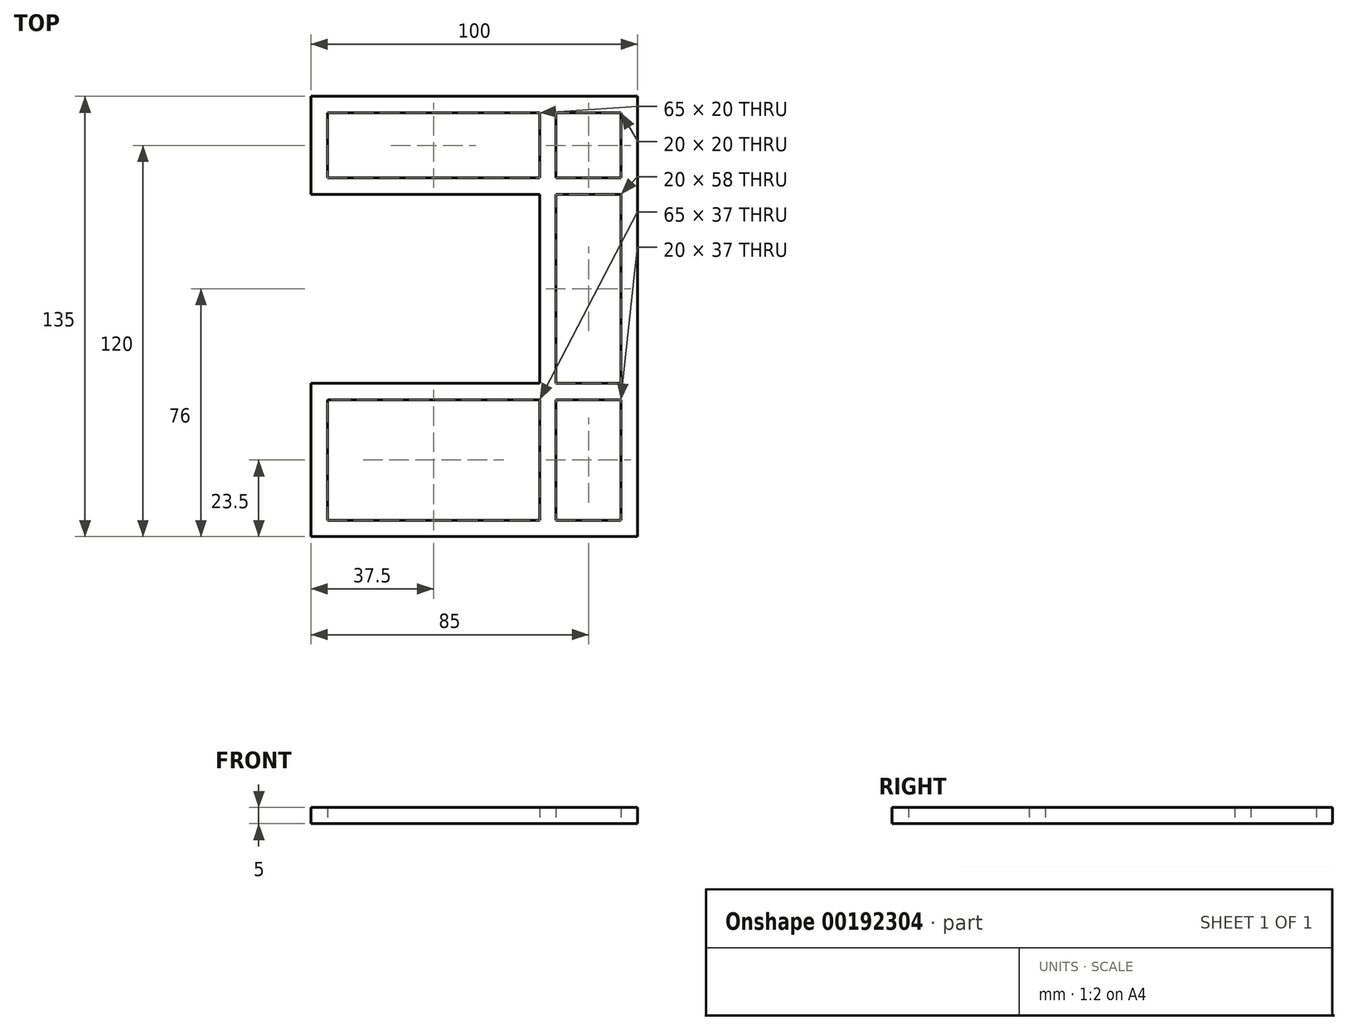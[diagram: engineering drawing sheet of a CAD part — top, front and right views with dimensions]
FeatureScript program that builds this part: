
annotation { "Feature Type Name" : "Feature", "Feature Type Description" : "" }
export const myFeature = defineFeature(function(context is Context, id is Id, definition is map)
    precondition{}
    {
        {
            var Q0;
            Q0=qCreatedBy(makeId("Top.planeOp"),FACE);
            var sketch = newSketch(context, id + "F0", { "sketchPlane" : qUnion([Q0])});
            skLineSegment(sketch, "E0", {"start": v(0, 0) * mm, "end": v(0, 135) * mm});
            skLineSegment(sketch, "E1", {"start": v(0, 135) * mm, "end": v(-100, 135) * mm});
            skLineSegment(sketch, "E2", {"start": v(-100, 135) * mm, "end": v(-100, 105) * mm});
            skLineSegment(sketch, "E3", {"start": v(-100, 105) * mm, "end": v(-30, 105) * mm});
            skLineSegment(sketch, "E4", {"start": v(0, 0) * mm, "end": v(-100, 0) * mm});
            skLineSegment(sketch, "E5", {"start": v(-100, 0) * mm, "end": v(-100, 47) * mm});
            skLineSegment(sketch, "E6", {"start": v(-100, 47) * mm, "end": v(-30, 47) * mm});
            skLineSegment(sketch, "E7", {"start": v(-30, 105) * mm, "end": v(-30, 47) * mm});
            skPoint(sketch, "E8.orphan", {"position": v(0, 47) * mm});
            skLineSegment(sketch, "E9.0", {"start": v(-95, 130) * mm, "end": v(-95, 110) * mm});
            skLineSegment(sketch, "E10.0", {"start": v(-5, 130) * mm, "end": v(-95, 130) * mm});
            skLineSegment(sketch, "E11.0", {"start": v(-5, 5) * mm, "end": v(-5, 130) * mm});
            skLineSegment(sketch, "E12.0", {"start": v(-5, 5) * mm, "end": v(-95, 5) * mm});
            skLineSegment(sketch, "E13.0", {"start": v(-95, 5) * mm, "end": v(-95, 42) * mm});
            skLineSegment(sketch, "E14.0", {"start": v(-95, 42) * mm, "end": v(-30, 42) * mm});
            skLineSegment(sketch, "E15.0", {"start": v(-25, 105) * mm, "end": v(-25, 47) * mm});
            skLineSegment(sketch, "E16.0", {"start": v(-95, 110) * mm, "end": v(-30, 110) * mm});
            skLineSegment(sketch, "E17", {"start": v(-25, 105) * mm, "end": v(-25, 110) * mm});
            skLineSegment(sketch, "E18", {"start": v(-30, 42) * mm, "end": v(-25, 42) * mm});
            skLineSegment(sketch, "E19", {"start": v(-25, 42) * mm, "end": v(-25, 47) * mm});
            skLineSegment(sketch, "E20", {"start": v(-25, 110) * mm, "end": v(-30, 110) * mm});
            skLineSegment(sketch, "E21", {"start": v(-5, 130) * mm, "end": v(-10, 130) * mm});
            skLineSegment(sketch, "E22", {"start": v(-5, 130) * mm, "end": v(-5, 125) * mm});
            skLineSegment(sketch, "E23", {"start": v(-30, 110) * mm, "end": v(-30, 130) * mm});
            skLineSegment(sketch, "E24", {"start": v(-25, 110) * mm, "end": v(-25, 130) * mm});
            skLineSegment(sketch, "E25", {"start": v(-30, 42) * mm, "end": v(-30, 5) * mm});
            skLineSegment(sketch, "E26", {"start": v(-25, 42) * mm, "end": v(-25, 5) * mm});
            skLineSegment(sketch, "E27", {"start": v(-25, 47) * mm, "end": v(-5, 47) * mm});
            skLineSegment(sketch, "E28", {"start": v(-25, 42) * mm, "end": v(-5, 42) * mm});
            skLineSegment(sketch, "E29", {"start": v(-25, 105) * mm, "end": v(-5, 105) * mm});
            skLineSegment(sketch, "E30", {"start": v(-25, 110) * mm, "end": v(-5, 110) * mm});
            skSolve(sketch);
        }
        {
            var Q0;
            Q0=makeQuery(id+"F0.imprint","IMPRINT",FACE,{"disambiguationData":[TD([[makeQuery(id+"F0.imprint","IMPRINT",EDGE,{"derivedFrom":sQuery(id+"F0.wireOp",EDGE,"E0")}),1.0]])]});
            var Q1;
            Q1=makeQuery(id+"F0.imprint","IMPRINT",FACE,{"disambiguationData":[TD([[makeQuery(id+"F0.imprint","IMPRINT",EDGE,{"derivedFrom":sQuery(id+"F0.wireOp",EDGE,"E20")}),-1.0]])]});
            var Q2;
            Q2=makeQuery(id+"F0.imprint","IMPRINT",FACE,{"disambiguationData":[TD([[makeQuery(id+"F0.imprint","IMPRINT",EDGE,{"derivedFrom":sQuery(id+"F0.wireOp",EDGE,"E17")}),-1.0]])]});
            var Q3;
            Q3=makeQuery(id+"F0.imprint","IMPRINT",FACE,{"disambiguationData":[TD([[makeQuery(id+"F0.imprint","IMPRINT",EDGE,{"derivedFrom":sQuery(id+"F0.wireOp",EDGE,"E19")}),-1.0]])]});
            var Q4;
            Q4=makeQuery(id+"F0.imprint","IMPRINT",FACE,{"disambiguationData":[TD([[makeQuery(id+"F0.imprint","IMPRINT",EDGE,{"derivedFrom":sQuery(id+"F0.wireOp",EDGE,"E18")}),-1.0]])]});
            extrude(context, id + "F1", {"entities" : qUnion([Q0, Q1, Q2, Q3, Q4]), "depth" : 5 * mm});
        }
    });
